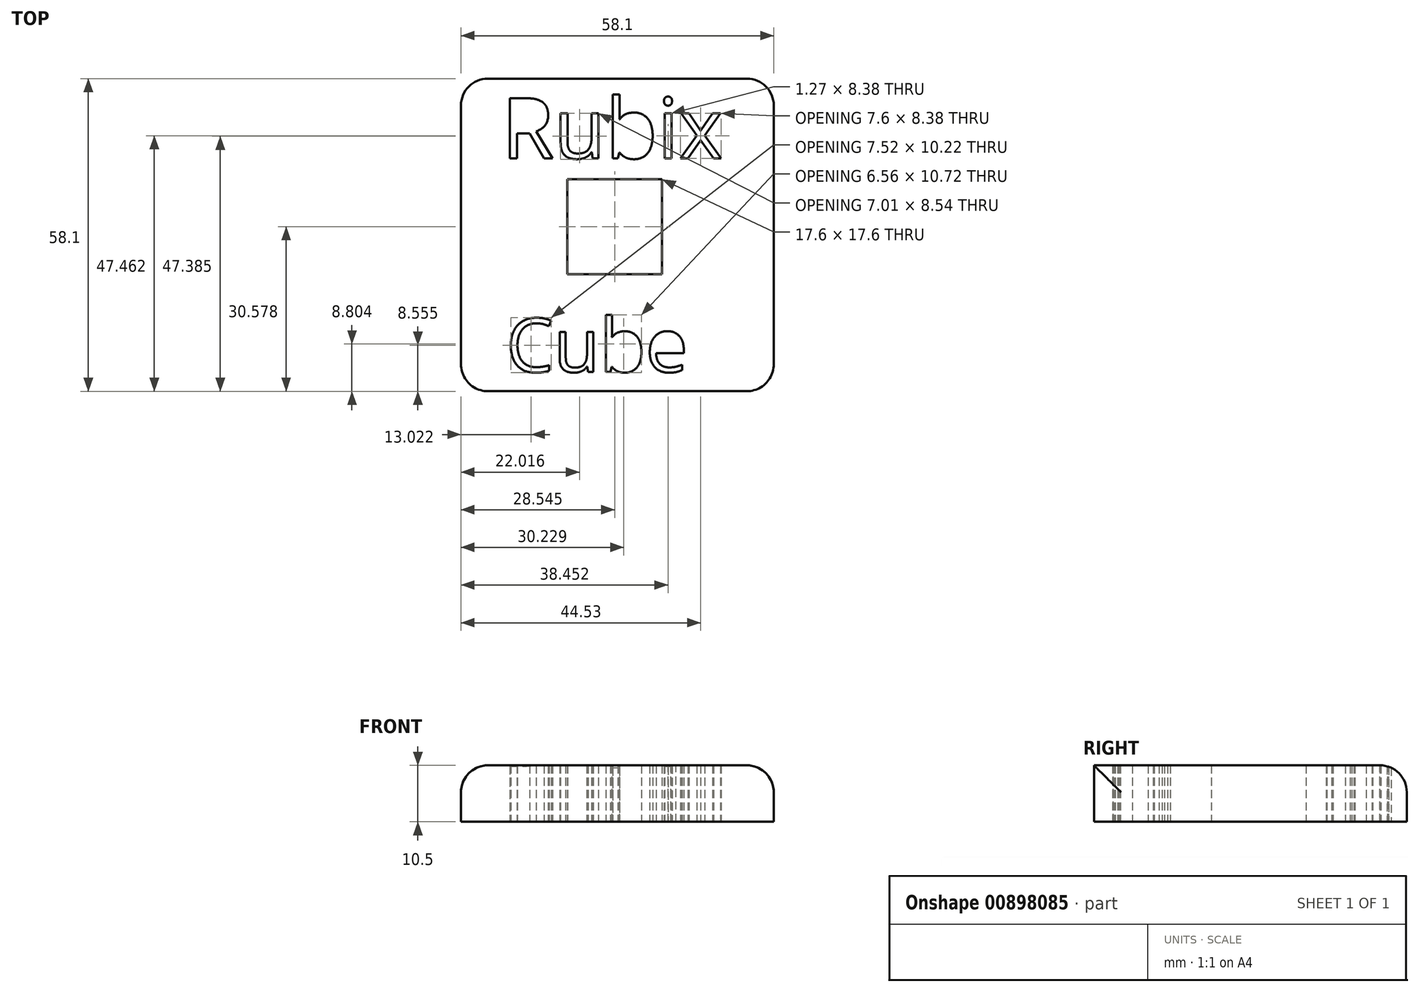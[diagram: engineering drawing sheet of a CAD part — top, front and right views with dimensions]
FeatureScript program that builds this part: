
annotation { "Feature Type Name" : "Feature", "Feature Type Description" : "" }
export const myFeature = defineFeature(function(context is Context, id is Id, definition is map)
    precondition{}
    {
        {
            var Q0;
            Q0=qCreatedBy(makeId("Top.planeOp"),FACE);
            var sketch = newSketch(context, id + "F0", { "sketchPlane" : qUnion([Q0])});
            skLineSegment(sketch, "E0.bottom", {"start": v(-41.44, 22.61) * mm, "end": v(16.66, 22.61) * mm});
            skLineSegment(sketch, "E0.top", {"start": v(-41.44, -35.49) * mm, "end": v(16.66, -35.49) * mm});
            skLineSegment(sketch, "E0.left", {"start": v(-41.44, 22.61) * mm, "end": v(-41.44, -35.49) * mm});
            skLineSegment(sketch, "E0.right", {"start": v(16.66, 22.61) * mm, "end": v(16.66, -35.49) * mm});
            skLineSegment(sketch, "E1.bottom", {"start": v(-21.7, 3.89) * mm, "end": v(-4.1, 3.89) * mm});
            skLineSegment(sketch, "E1.top", {"start": v(-21.7, -13.71) * mm, "end": v(-4.1, -13.71) * mm});
            skLineSegment(sketch, "E1.left", {"start": v(-21.7, 3.89) * mm, "end": v(-21.7, -13.71) * mm});
            skLineSegment(sketch, "E1.right", {"start": v(-4.1, 3.89) * mm, "end": v(-4.1, -13.71) * mm});
            skText(sketch, "E2", { "text": "Rubix", "fontName": "OpenSans-Regular.ttf"});
            skText(sketch, "E3", { "text": "Cube", "fontName": "OpenSans-Regular.ttf"});
            const initialGuessF0  = {"E2": [-0.03387, 0.00778, 1, 0, 0.01128], "E3": [-0.03303, -0.03191, 1, 0, 0.01003]};
            skSetInitialGuess(sketch, initialGuessF0);
            skSolve(sketch);
        }
        {
            var Q0;
            Q0=makeQuery(id+"F0.imprint","IMPRINT",FACE,{"disambiguationData":[TD([[makeQuery(id+"F0.imprint","IMPRINT",EDGE,{"derivedFrom":sQuery(id+"F0.wireOp",EDGE,"E0.bottom")}),-1.0]])]});
            extrude(context, id + "F1", {"entities" : qUnion([Q0]), "depth" : 10.5 * mm, "offsetDistance" : 25 * mm});
        }
        {
            var Q0;
            Q0=makeQuery(id+"F1.opExtrude","CAP_EDGE",EDGE,{"disambiguationData":[OSD([sQuery(id+"F0.wireOp",EDGE,"E0.bottom")])],"isStart":false});
            var Q1;
            Q1=makeQuery(id+"F1.opExtrude","CAP_EDGE",EDGE,{"disambiguationData":[OSD([sQuery(id+"F0.wireOp",EDGE,"E0.right")])],"isStart":false});
            var Q2;
            Q2=makeQuery(id+"F1.opExtrude","CAP_EDGE",EDGE,{"disambiguationData":[OSD([sQuery(id+"F0.wireOp",EDGE,"E0.left")])],"isStart":false});
            var Q3;
            Q3=makeQuery(id+"F1.opExtrude","SWEPT_EDGE",EDGE,{"disambiguationData":[OSD([sQuery(id+"F0.wireOp",EDGE,"E0.top"),sQuery(id+"F0.wireOp",EDGE,"E0.right")])]});
            var Q4;
            Q4=makeQuery(id+"F1.opExtrude","SWEPT_EDGE",EDGE,{"disambiguationData":[OSD([sQuery(id+"F0.wireOp",EDGE,"E0.top"),sQuery(id+"F0.wireOp",EDGE,"E0.left")])]});
            var Q5;
            Q5=makeQuery(id+"F1.opExtrude","SWEPT_EDGE",EDGE,{"disambiguationData":[OSD([sQuery(id+"F0.wireOp",EDGE,"E0.bottom"),sQuery(id+"F0.wireOp",EDGE,"E0.right")])]});
            var Q6;
            Q6=makeQuery(id+"F1.opExtrude","SWEPT_EDGE",EDGE,{"disambiguationData":[OSD([sQuery(id+"F0.wireOp",EDGE,"E0.bottom"),sQuery(id+"F0.wireOp",EDGE,"E0.left")])]});
            fillet(context, id + "F2", {"entities" : qUnion([Q0, Q1, Q2, Q3, Q4, Q5, Q6]), "radius" : 5 * mm, "tangentPropagation" : true, "allowEdgeOverflow" : false});
        }
    });
